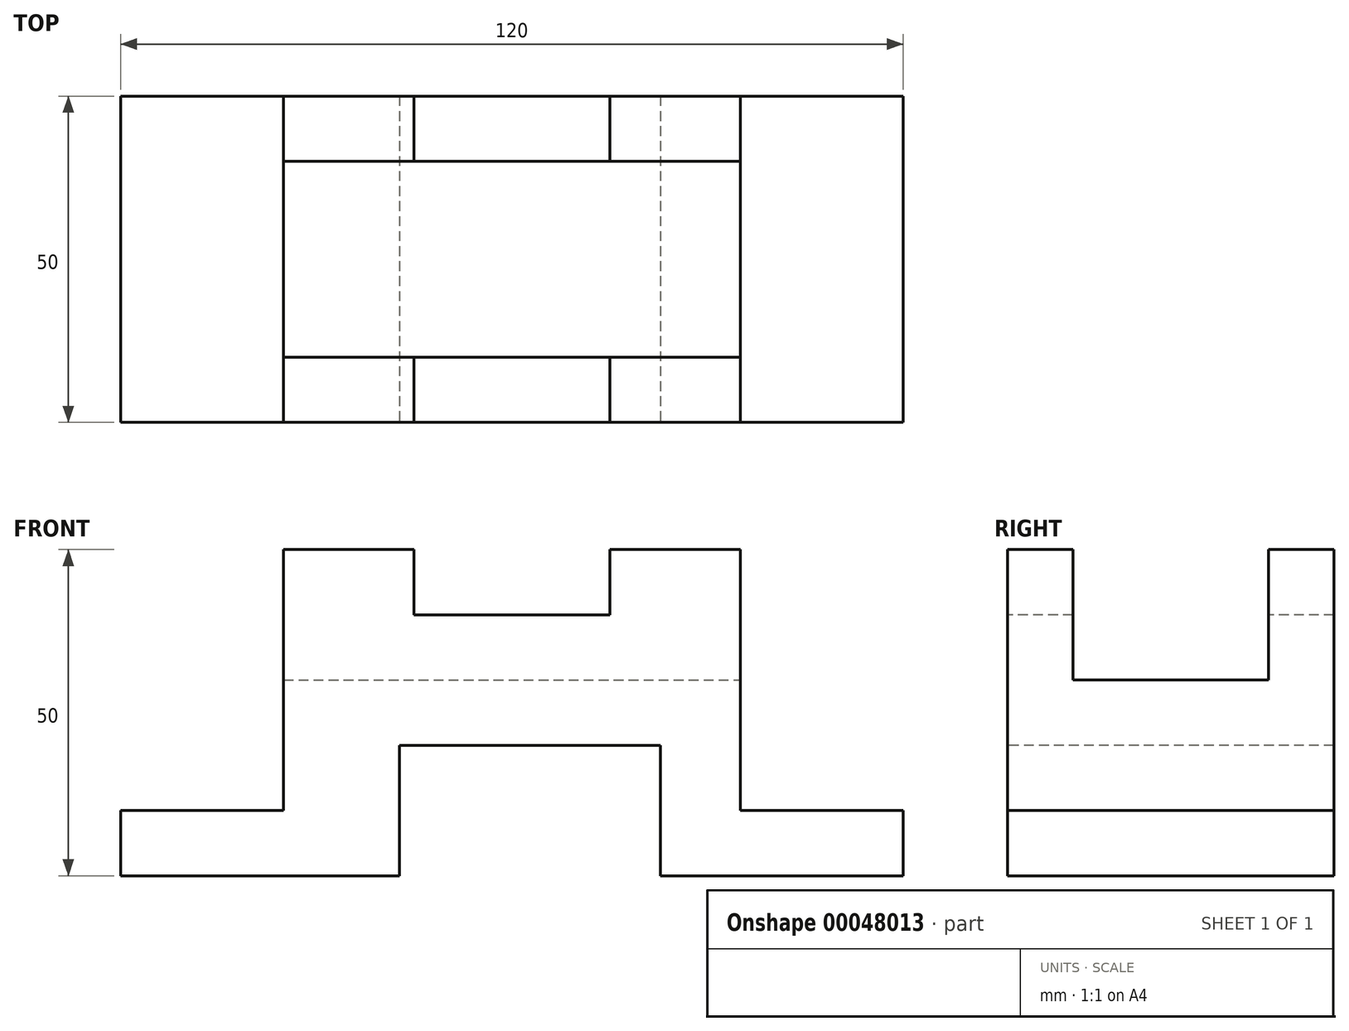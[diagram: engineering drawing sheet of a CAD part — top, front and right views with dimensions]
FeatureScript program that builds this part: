
annotation { "Feature Type Name" : "Feature", "Feature Type Description" : "" }
export const myFeature = defineFeature(function(context is Context, id is Id, definition is map)
    precondition{}
    {
        {
            var Q0;
            Q0=qCreatedBy(makeId("Front.planeOp"),FACE);
            var sketch = newSketch(context, id + "F0", { "sketchPlane" : qUnion([Q0])});
            skLineSegment(sketch, "E0.bottom", {"start": v(-82.75, 30) * mm, "end": v(37.25, 30) * mm});
            skLineSegment(sketch, "E0.top", {"start": v(-82.75, -20) * mm, "end": v(37.25, -20) * mm});
            skLineSegment(sketch, "E0.left", {"start": v(-82.75, 30) * mm, "end": v(-82.75, -20) * mm});
            skLineSegment(sketch, "E0.right", {"start": v(37.25, 30) * mm, "end": v(37.25, -20) * mm});
            skLineSegment(sketch, "E1", {"start": v(-40, -20) * mm, "end": v(-40, 0) * mm});
            skLineSegment(sketch, "E2", {"start": v(-40, 0) * mm, "end": v(0, 0) * mm});
            skLineSegment(sketch, "E3", {"start": v(0, 0) * mm, "end": v(0, -20) * mm});
            skLineSegment(sketch, "E4", {"start": v(-82.75, -10) * mm, "end": v(-57.75, -10) * mm});
            skLineSegment(sketch, "E5", {"start": v(-57.75, -10) * mm, "end": v(-57.75, 30) * mm});
            skLineSegment(sketch, "E6", {"start": v(-22.75, 30) * mm, "end": v(-22.75, -20) * mm, "construction": true});
            skLineSegment(sketch, "E7.MirrorCS", {"start": v(37.25, -10) * mm, "end": v(12.25, -10) * mm});
            skLineSegment(sketch, "E8.MirrorCS", {"start": v(12.25, -10) * mm, "end": v(12.25, 30) * mm});
            skLineSegment(sketch, "E9", {"start": v(-37.75, 30) * mm, "end": v(-37.75, 20) * mm});
            skLineSegment(sketch, "E10", {"start": v(-37.75, 20) * mm, "end": v(-7.75, 20) * mm});
            skLineSegment(sketch, "E11", {"start": v(-7.75, 20) * mm, "end": v(-7.75, 30) * mm});
            skSolve(sketch);
        }
        {
            var Q0;
            {var subQ6=sQuery(id+"F0.wireOp",EDGE,"E1");Q0=makeQuery(id+"F0.imprint","IMPRINT",FACE,{"disambiguationData":[TD([[makeQuery(id+"F0.imprint","IMPRINT",EDGE,{"derivedFrom":subQ6}),1.0]])]});}
            extrude(context, id + "F1", {"entities" : qUnion([Q0]), "oppositeDirection" : true, "depth" : 50 * mm});
        }
        {
            var Q0;
            {var subQ0=sQuery(id+"F0.wireOp",EDGE,"E0.bottom");Q0=makeQuery(id+"F1.opExtrude","SWEPT_FACE",FACE,{"disambiguationData":[OSD([subQ0]),TDD([makeQuery(id+"F0.imprint","IMPRINT",EDGE,{"disambiguationData":[TD([[makeQuery(id+"F0.imprint","INTERSECT",VERTEX,{"derivedFrom":[subQ0,sQuery(id+"F0.wireOp",EDGE,"E5")]}),-1.0]])],"derivedFrom":subQ0})])]});}
            var sketch = newSketch(context, id + "F2", { "sketchPlane" : qUnion([Q0])});
            skLineSegment(sketch, "E12.bottom", {"start": v(-57.75, 10) * mm, "end": v(12.25, 10) * mm});
            skLineSegment(sketch, "E12.top", {"start": v(-57.75, 40) * mm, "end": v(12.25, 40) * mm});
            skLineSegment(sketch, "E12.left", {"start": v(-57.75, 10) * mm, "end": v(-57.75, 40) * mm});
            skLineSegment(sketch, "E12.right", {"start": v(12.25, 10) * mm, "end": v(12.25, 40) * mm});
            skSolve(sketch);
        }
        {
            var Q0;
            Q0 = qSketchRegion(id + "F2", true);
            extrude(context, id + "F3", {"entities" : qUnion([Q0]), "operationType" : NewBodyOperationType.REMOVE, "oppositeDirection" : true, "depth" : 20 * mm});
        }
    });
